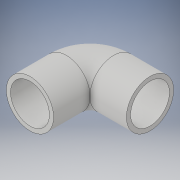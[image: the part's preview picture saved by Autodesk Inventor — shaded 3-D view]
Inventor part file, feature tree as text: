
AUTODESK INVENTOR PART (.ipt)
format: ipt  version: 2018 (Build 220112000, 112)  size: 182,784 bytes
history: native  units: in
note: dims shown in document units (in); Inventor stores cm internally (conversion verified against a paired STEP export)
features: sketch x6, extrude x4, plane x3, revolve x2, other x1
ambient origin geometry x8: Origin, YZ Plane, XZ Plane, XY Plane, X Axis, Y Axis, Z Axis, Center Point
bodies: Solid1 (feature_tree)
feature tree (16):
  extrude  "Extrusion1"  Depth=1.237in TaperAngle=0.0deg
  sketch  "Sketch2"  dims[d3=-0.6184in d4=0.8025in]
  plane  "Work Plane1"
  extrude  "Extrusion2"  Depth=0.8025in
  sketch  "Sketch4"  dims[d8=1.321in d9=0.0in]
  sketch  "Sketch5"  dims[d10=0.0in d11=90.0deg]
  plane  "Work Plane2"
  plane  "Work Plane3"
  revolve  "Revolution1"  [1 undecoded]
  extrude  "Extrusion3"  TaperAngle=0.0deg  [1 undecoded]
  other  "Work Axis1"
  revolve  "Revolution2"  Angle=90.0deg
  extrude  "Extrusion4"  Depth=1.25in
  sketch  "Sketch1"  dims[d0=1.605in d1=1.237in d2=0.0in]
  sketch  "Sketch3"  dims[d5=1.237in d6=0.0in d7=1.321in]
  sketch  "Sketch6"  dims[d12=1.25in d13=0.0in d14=1.0in d15=90.0deg d16=1.25in d17=0.0in]
note: 2 required parameter values undecoded (feature->parameter linkage not recoverable at this tier; creation-order binding heuristic only, values carry confidence <= 0.55)